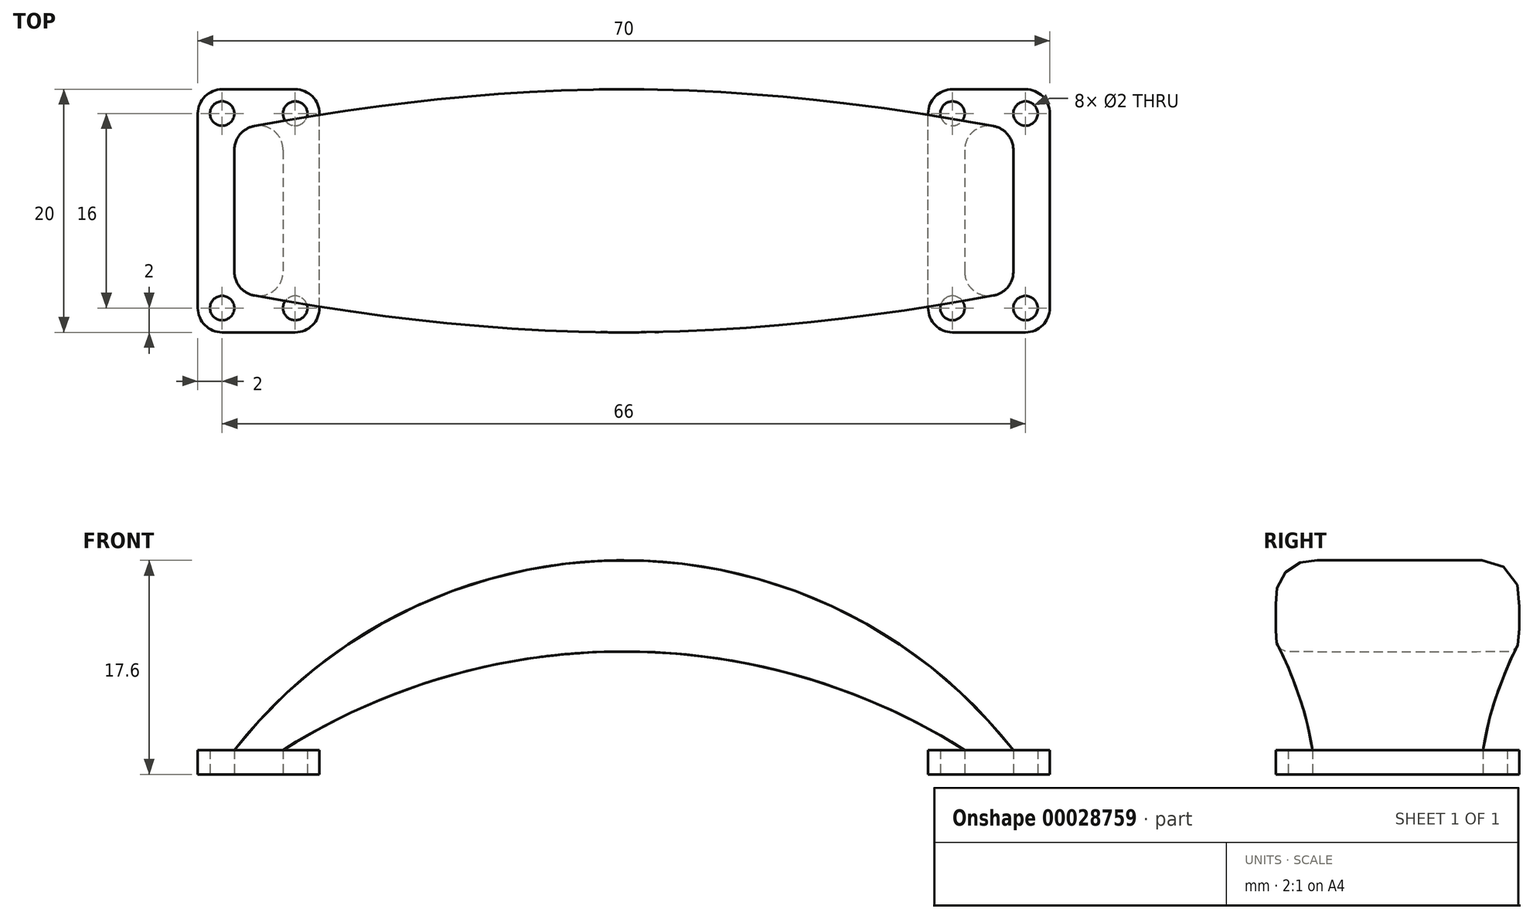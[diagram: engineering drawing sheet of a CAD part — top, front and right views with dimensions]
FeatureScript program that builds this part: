
annotation { "Feature Type Name" : "Feature", "Feature Type Description" : "" }
export const myFeature = defineFeature(function(context is Context, id is Id, definition is map)
    precondition{}
    {
        {
            var Q0;
            Q0=qCreatedBy(makeId("Right.planeOp"),FACE);
            var sketch = newSketch(context, id + "F0", { "sketchPlane" : qUnion([Q0])});
            skLineSegment(sketch, "E0", {"start": v(-7, 17.6) * mm, "end": v(7, 17.6) * mm});
            skLineSegment(sketch, "E1", {"start": v(10, 14.6) * mm, "end": v(10, 11.1) * mm});
            skLineSegment(sketch, "E2", {"start": v(9, 10.1) * mm, "end": v(-9, 10.1) * mm});
            skLineSegment(sketch, "E3", {"start": v(-10, 11.1) * mm, "end": v(-10, 14.6) * mm});
            skLineSegment(sketch, "E4", {"start": v(0, 21.16) * mm, "end": v(0, -4.4) * mm, "construction": true});
            skPoint(sketch, "E5.visualSharp", {"position": v(-10, 17.6) * mm});
            skArc(sketch, "E5.filletArc", {"start": v(-7, 17.6) * mm, "mid": v(-9.12, 16.73) * mm, "end": v(-10, 14.6) * mm});
            skPoint(sketch, "E6.visualSharp", {"position": v(10, 17.6) * mm});
            skArc(sketch, "E6.filletArc", {"start": v(10, 14.6) * mm, "mid": v(9.12, 16.73) * mm, "end": v(7, 17.6) * mm});
            skPoint(sketch, "E7.visualSharp", {"position": v(-10, 10.1) * mm});
            skArc(sketch, "E7.filletArc", {"start": v(-10, 11.1) * mm, "mid": v(-9.7, 10.4) * mm, "end": v(-9, 10.1) * mm});
            skPoint(sketch, "E8.visualSharp", {"position": v(10, 10.1) * mm});
            skArc(sketch, "E8.filletArc", {"start": v(9, 10.1) * mm, "mid": v(9.7, 10.4) * mm, "end": v(10, 11.1) * mm});
            skSolve(sketch);
        }
        {
            var Q0;
            Q0=qCreatedBy(makeId("Top.planeOp"),FACE);
            var sketch = newSketch(context, id + "F1", { "sketchPlane" : qUnion([Q0])});
            skLineSegment(sketch, "E9", {"start": v(35, -20.47) * mm, "end": v(35, 19.34) * mm, "construction": true});
            skLineSegment(sketch, "E10.bottom", {"start": v(33, -10) * mm, "end": v(27, -10) * mm});
            skLineSegment(sketch, "E10.top", {"start": v(33, 10) * mm, "end": v(27, 10) * mm});
            skLineSegment(sketch, "E10.left", {"start": v(35, -8) * mm, "end": v(35, 8) * mm});
            skLineSegment(sketch, "E10.right", {"start": v(25, -8) * mm, "end": v(25, 8) * mm});
            skLineSegment(sketch, "E11", {"start": v(35.63, 0) * mm, "end": v(-81.9, 0) * mm, "construction": true});
            skCircle(sketch, "E12", {"center": v(33, -8) * mm, "radius": 1 * mm});
            skCircle(sketch, "E13", {"center": v(27, -8) * mm, "radius": 1 * mm});
            skCircle(sketch, "E14", {"center": v(33, 8) * mm, "radius": 1 * mm});
            skCircle(sketch, "E15", {"center": v(27, 8) * mm, "radius": 1 * mm});
            skPoint(sketch, "E16.visualSharp", {"position": v(25, -10) * mm});
            skArc(sketch, "E16.filletArc", {"start": v(25, -8) * mm, "mid": v(25.59, -9.41) * mm, "end": v(27, -10) * mm});
            skPoint(sketch, "E17.visualSharp", {"position": v(25, 10) * mm});
            skArc(sketch, "E17.filletArc", {"start": v(27, 10) * mm, "mid": v(25.59, 9.41) * mm, "end": v(25, 8) * mm});
            skPoint(sketch, "E18.visualSharp", {"position": v(35, 10) * mm});
            skArc(sketch, "E18.filletArc", {"start": v(35, 8) * mm, "mid": v(34.41, 9.41) * mm, "end": v(33, 10) * mm});
            skPoint(sketch, "E19.visualSharp", {"position": v(35, -10) * mm});
            skArc(sketch, "E19.filletArc", {"start": v(33, -10) * mm, "mid": v(34.41, -9.41) * mm, "end": v(35, -8) * mm});
            skLineSegment(sketch, "E20", {"start": v(35, -8) * mm, "end": v(25, -8) * mm, "construction": true});
            skLineSegment(sketch, "E21", {"start": v(33, -10) * mm, "end": v(33, 10) * mm, "construction": true});
            skLineSegment(sketch, "E22", {"start": v(35, 8) * mm, "end": v(25, 8) * mm, "construction": true});
            skLineSegment(sketch, "E23", {"start": v(27, -10) * mm, "end": v(27, 10) * mm, "construction": true});
            skCircle(sketch, "E24", {"center": v(-33, -8) * mm, "radius": 1 * mm});
            skLineSegment(sketch, "E25.bottom", {"start": v(-27, -10) * mm, "end": v(-33, -10) * mm});
            skLineSegment(sketch, "E25.right", {"start": v(-35, -8) * mm, "end": v(-35, 8) * mm});
            skLineSegment(sketch, "E26", {"start": v(-25, 8) * mm, "end": v(-35, 8) * mm, "construction": true});
            skLineSegment(sketch, "E27", {"start": v(-33, -10) * mm, "end": v(-33, 10) * mm, "construction": true});
            skPoint(sketch, "E28.visualSharp", {"position": v(-35, -10) * mm});
            skLineSegment(sketch, "E25.top", {"start": v(-27, 10) * mm, "end": v(-33, 10) * mm});
            skPoint(sketch, "E29.visualSharp", {"position": v(-25, -10) * mm});
            skPoint(sketch, "E30.visualSharp", {"position": v(-25, 10) * mm});
            skLineSegment(sketch, "E31", {"start": v(-27, -10) * mm, "end": v(-27, 10) * mm, "construction": true});
            skLineSegment(sketch, "E32", {"start": v(-25, -8) * mm, "end": v(-35, -8) * mm, "construction": true});
            skLineSegment(sketch, "E25.left", {"start": v(-25, -8) * mm, "end": v(-25, 8) * mm});
            skPoint(sketch, "E33.visualSharp", {"position": v(-35, 10) * mm});
            skCircle(sketch, "E34", {"center": v(-27, -8) * mm, "radius": 1 * mm});
            skArc(sketch, "E30.filletArc", {"start": v(-25, 8) * mm, "mid": v(-25.59, 9.41) * mm, "end": v(-27, 10) * mm});
            skArc(sketch, "E33.filletArc", {"start": v(-33, 10) * mm, "mid": v(-34.41, 9.41) * mm, "end": v(-35, 8) * mm});
            skArc(sketch, "E29.filletArc", {"start": v(-27, -10) * mm, "mid": v(-25.59, -9.41) * mm, "end": v(-25, -8) * mm});
            skCircle(sketch, "E35", {"center": v(-27, 8) * mm, "radius": 1 * mm});
            skCircle(sketch, "E36", {"center": v(-33, 8) * mm, "radius": 1 * mm});
            skArc(sketch, "E28.filletArc", {"start": v(-35, -8) * mm, "mid": v(-34.41, -9.41) * mm, "end": v(-33, -10) * mm});
            skSolve(sketch);
        }
        {
            var Q0;
            Q0=makeQuery(id+"F1.imprint","IMPRINT",FACE,{"disambiguationData":[TD([[makeQuery(id+"F1.imprint","IMPRINT",EDGE,{"derivedFrom":sQuery(id+"F1.wireOp",EDGE,"E24")}),-1.0]])]});
            var Q1;
            Q1=makeQuery(id+"F1.imprint","IMPRINT",FACE,{"disambiguationData":[TD([[makeQuery(id+"F1.imprint","IMPRINT",EDGE,{"derivedFrom":sQuery(id+"F1.wireOp",EDGE,"E10.bottom")}),-1.0]])]});
            extrude(context, id + "F2", {"entities" : qUnion([Q0, Q1]), "depth" : 2 * mm});
        }
        {
            var Q0;
            Q0=makeQuery(id+"F2.opExtrude","CAP_FACE",FACE,{"disambiguationData":[OSD([sQuery(id+"F1.wireOp",EDGE,"E24"),sQuery(id+"F1.wireOp",EDGE,"E25.bottom"),sQuery(id+"F1.wireOp",EDGE,"E25.right"),sQuery(id+"F1.wireOp",EDGE,"E25.top"),sQuery(id+"F1.wireOp",EDGE,"E25.left"),sQuery(id+"F1.wireOp",EDGE,"E34"),sQuery(id+"F1.wireOp",EDGE,"E30.filletArc"),sQuery(id+"F1.wireOp",EDGE,"E33.filletArc"),sQuery(id+"F1.wireOp",EDGE,"E29.filletArc"),sQuery(id+"F1.wireOp",EDGE,"E35"),sQuery(id+"F1.wireOp",EDGE,"E36"),sQuery(id+"F1.wireOp",EDGE,"E28.filletArc")])],"isStart":false});
            cPlane(context, id + "F3", {"entities" : qUnion([Q0]), "cplaneType" : CPlaneType.OFFSET, "offset" : 0 * mm, "width" : 150 * mm, "height" : 150 * mm});
        }
        {
            var Q0;
            Q0=qCreatedBy(id+"F3.planeOp",FACE);
            var sketch = newSketch(context, id + "F4", { "sketchPlane" : qUnion([Q0])});
            skLineSegment(sketch, "E37", {"start": v(-32, 5) * mm, "end": v(-32, -5) * mm});
            skLineSegment(sketch, "E38", {"start": v(-28, 5) * mm, "end": v(-28, -5) * mm});
            skLineSegment(sketch, "E39", {"start": v(-30, 7) * mm, "end": v(-30, 7) * mm});
            skLineSegment(sketch, "E40", {"start": v(-30, -7) * mm, "end": v(-30, -7) * mm});
            skArc(sketch, "E41.filletArc", {"start": v(-30, 7) * mm, "mid": v(-31.41, 6.42) * mm, "end": v(-32, 5) * mm});
            skArc(sketch, "E42.filletArc", {"start": v(-28, 5) * mm, "mid": v(-28.58, 6.42) * mm, "end": v(-30, 7) * mm});
            skArc(sketch, "E43.filletArc", {"start": v(-30, -7) * mm, "mid": v(-28.58, -6.42) * mm, "end": v(-28, -5) * mm});
            skArc(sketch, "E44.filletArc", {"start": v(-32, -5) * mm, "mid": v(-31.41, -6.42) * mm, "end": v(-30, -7) * mm});
            skLineSegment(sketch, "E45", {"start": v(-32, -5) * mm, "end": v(-32, -12.76) * mm, "construction": true});
            skLineSegment(sketch, "E46", {"start": v(-32, 5) * mm, "end": v(-32, 11.8) * mm, "construction": true});
            skSolve(sketch);
        }
        {
            var Q0;
            Q0=qCreatedBy(id+"F3.planeOp",FACE);
            var sketch = newSketch(context, id + "F5", { "sketchPlane" : qUnion([Q0])});
            skLineSegment(sketch, "E47", {"start": v(28, 5) * mm, "end": v(28, -5) * mm});
            skLineSegment(sketch, "E48", {"start": v(32, 5) * mm, "end": v(32, -5) * mm});
            skLineSegment(sketch, "E49", {"start": v(30, -7) * mm, "end": v(30, -7) * mm});
            skLineSegment(sketch, "E50", {"start": v(30, 7) * mm, "end": v(30, 7) * mm});
            skArc(sketch, "E51.filletArc", {"start": v(30, 7) * mm, "mid": v(28.59, 6.41) * mm, "end": v(28, 5) * mm});
            skArc(sketch, "E52.filletArc", {"start": v(32, 5) * mm, "mid": v(31.42, 6.41) * mm, "end": v(30, 7) * mm});
            skArc(sketch, "E53.filletArc", {"start": v(28, -5) * mm, "mid": v(28.59, -6.42) * mm, "end": v(30, -7) * mm});
            skArc(sketch, "E54.filletArc", {"start": v(30, -7) * mm, "mid": v(31.42, -6.42) * mm, "end": v(32, -5) * mm});
            skSolve(sketch);
        }
        {
            var Q0;
            Q0=sQuery(id+"F4.wireOp",VERTEX,"E45.start");
            var Q1;
            Q1=sQuery(id+"F4.wireOp",EDGE,"E45");
            cPlane(context, id + "F6", {"entities" : qUnion([Q0, Q1]), "cplaneType" : CPlaneType.LINE_POINT, "offset" : 150 * mm, "width" : 150 * mm, "height" : 150 * mm});
        }
        {
            var Q0;
            Q0=sQuery(id+"F4.wireOp",VERTEX,"E41.filletArc.end");
            var Q1;
            Q1=sQuery(id+"F4.wireOp",EDGE,"E46");
            cPlane(context, id + "F7", {"entities" : qUnion([Q0, Q1]), "cplaneType" : CPlaneType.LINE_POINT, "offset" : 150 * mm, "width" : 150 * mm, "height" : 150 * mm});
        }
        {
            var Q0;
            Q0=qCreatedBy(id+"F6.planeOp",FACE);
            var sketch = newSketch(context, id + "F8", { "sketchPlane" : qUnion([Q0])});
            skArc(sketch, "E55", {"start": v(32, 2) * mm, "mid": v(0, 17.6) * mm, "end": v(-32, 2) * mm});
            skPoint(sketch, "E55.first.point", {"position": v(-32, 2) * mm});
            skPoint(sketch, "E55.second.point", {"position": v(0, 17.6) * mm});
            skPoint(sketch, "E55.third.point", {"position": v(32, 2) * mm});
            skSolve(sketch);
        }
        {
            var Q0;
            Q0=qCreatedBy(id+"F6.planeOp",FACE);
            var sketch = newSketch(context, id + "F9", { "sketchPlane" : qUnion([Q0])});
            skArc(sketch, "E56", {"start": v(28, 2) * mm, "mid": v(0, 10.1) * mm, "end": v(-28, 2) * mm});
            skPoint(sketch, "E56.first.point", {"position": v(-28, 2) * mm});
            skPoint(sketch, "E56.second.point", {"position": v(0, 10.1) * mm});
            skPoint(sketch, "E56.third.point", {"position": v(28, 2) * mm});
            skSolve(sketch);
        }
        {
            var Q0;
            Q0=qCreatedBy(id+"F7.planeOp",FACE);
            var sketch = newSketch(context, id + "F10", { "sketchPlane" : qUnion([Q0])});
            skArc(sketch, "E57", {"start": v(32, 2) * mm, "mid": v(0, 17.6) * mm, "end": v(-32, 2) * mm});
            skPoint(sketch, "E57.first.point", {"position": v(-32, 2) * mm});
            skPoint(sketch, "E57.second.point", {"position": v(0, 17.6) * mm});
            skPoint(sketch, "E57.third.point", {"position": v(32, 2) * mm});
            skSolve(sketch);
        }
        {
            var Q0;
            Q0=qCreatedBy(id+"F7.planeOp",FACE);
            var sketch = newSketch(context, id + "F11", { "sketchPlane" : qUnion([Q0])});
            skArc(sketch, "E58", {"start": v(28, 2) * mm, "mid": v(0, 10.1) * mm, "end": v(-28, 2) * mm});
            skPoint(sketch, "E58.first.point", {"position": v(-28, 2) * mm});
            skPoint(sketch, "E58.second.point", {"position": v(0, 10.1) * mm});
            skPoint(sketch, "E58.third.point", {"position": v(28, 2) * mm});
            skSolve(sketch);
        }
        {
            var Q0;
            Q0=makeQuery(id+"F5.imprint","IMPRINT",FACE,{"disambiguationData":[TD([[makeQuery(id+"F5.imprint","IMPRINT",EDGE,{"derivedFrom":sQuery(id+"F5.wireOp",EDGE,"E47")}),1.0]])]});
            var Q1;
            Q1=makeQuery(id+"F0.imprint","IMPRINT",FACE,{"disambiguationData":[TD([[makeQuery(id+"F0.imprint","IMPRINT",EDGE,{"derivedFrom":sQuery(id+"F0.wireOp",EDGE,"E0")}),-1.0]])]});
            var Q2;
            Q2=makeQuery(id+"F4.imprint","IMPRINT",FACE,{"disambiguationData":[TD([[makeQuery(id+"F4.imprint","IMPRINT",EDGE,{"derivedFrom":sQuery(id+"F4.wireOp",EDGE,"E37")}),1.0]])]});
            var Q3;
            Q3=sQuery(id+"F8.wireOp",EDGE,"E55");
            var Q4;
            Q4=sQuery(id+"F10.wireOp",EDGE,"E57");
            var Q5;
            Q5=sQuery(id+"F11.wireOp",EDGE,"E58");
            var Q6;
            Q6=sQuery(id+"F9.wireOp",EDGE,"E56");
            loft(context, id + "F12", {"addGuides" : true, "sheetProfilesArray" : [{ "sheetProfileEntities" : qUnion([Q0]) }, { "sheetProfileEntities" : qUnion([Q1]) }, { "sheetProfileEntities" : qUnion([Q2]) }], "guidesArray" : [{ "guideEntities" : qUnion([Q3]), "guideDerivativeType" : LoftGuideDerivativeType.DEFAULT, "guideDerivativeMagnitude" : 1 }, { "guideEntities" : qUnion([Q4]), "guideDerivativeType" : LoftGuideDerivativeType.DEFAULT, "guideDerivativeMagnitude" : 1 }, { "guideEntities" : qUnion([Q5]), "guideDerivativeType" : LoftGuideDerivativeType.DEFAULT, "guideDerivativeMagnitude" : 1 }, { "guideEntities" : qUnion([Q6]), "guideDerivativeType" : LoftGuideDerivativeType.DEFAULT, "guideDerivativeMagnitude" : 1 }]});
        }
    });
